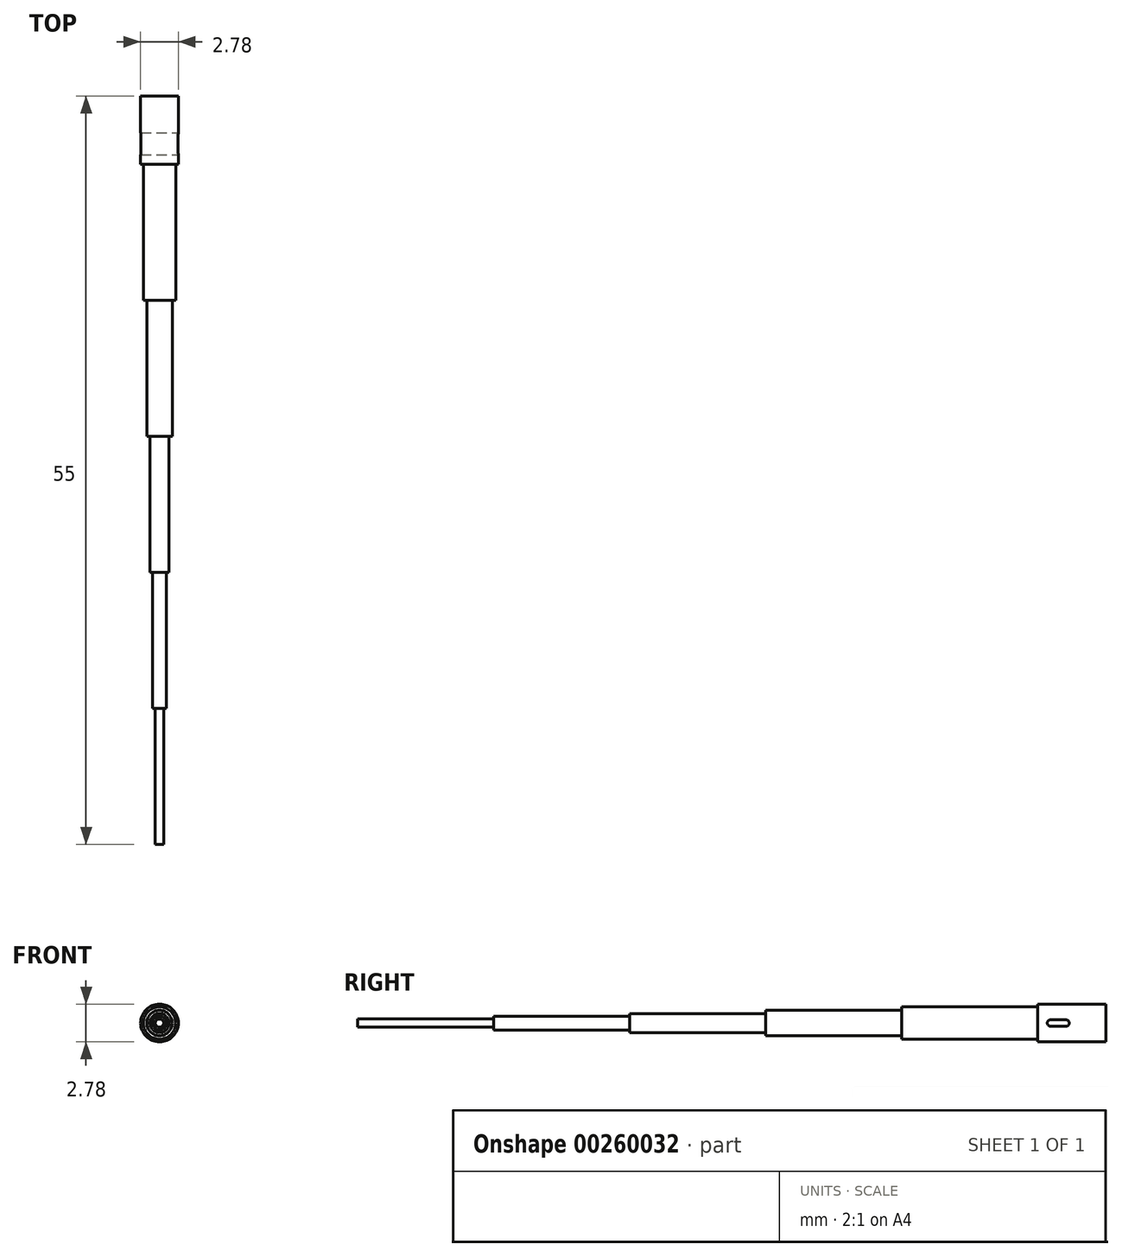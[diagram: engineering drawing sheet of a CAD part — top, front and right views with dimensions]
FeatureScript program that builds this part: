
annotation { "Feature Type Name" : "Feature", "Feature Type Description" : "" }
export const myFeature = defineFeature(function(context is Context, id is Id, definition is map)
    precondition{}
    {
        {
            var Q0;
            Q0=qCreatedBy(makeId("Front.planeOp"),FACE);
            var sketch = newSketch(context, id + "F0", { "sketchPlane" : qUnion([Q0])});
            skCircle(sketch, "E0", {"center": v(0, 0) * mm, "radius": 1.39 * mm});
            skSolve(sketch);
        }
        {
            var Q0;
            Q0 = qSketchRegion(id + "F0", true);
            extrude(context, id + "F1", {"entities" : qUnion([Q0]), "depth" : 5 * mm});
        }
        {
            var Q0;
            Q0=makeQuery(id+"F1.opExtrude","CAP_FACE",FACE,{"disambiguationData":[OSD([sQuery(id+"F0.wireOp",EDGE,"E0")])],"isStart":false});
            var sketch = newSketch(context, id + "F2", { "sketchPlane" : qUnion([Q0])});
            skCircle(sketch, "E1", {"center": v(0, 0) * mm, "radius": 1.19 * mm});
            skSolve(sketch);
        }
        {
            var Q0;
            Q0 = qSketchRegion(id + "F2", true);
            extrude(context, id + "F3", {"entities" : qUnion([Q0]), "operationType" : NewBodyOperationType.ADD, "depth" : 10 * mm});
        }
        {
            var Q0;
            Q0=makeQuery(id+"F3.opExtrude","CAP_FACE",FACE,{"disambiguationData":[OSD([sQuery(id+"F2.wireOp",EDGE,"E1")])],"isStart":false});
            var sketch = newSketch(context, id + "F4", { "sketchPlane" : qUnion([Q0])});
            skCircle(sketch, "E2", {"center": v(0, 0) * mm, "radius": 0.93 * mm});
            skSolve(sketch);
        }
        {
            var Q0;
            Q0 = qSketchRegion(id + "F4", true);
            extrude(context, id + "F5", {"entities" : qUnion([Q0]), "operationType" : NewBodyOperationType.ADD, "depth" : 10 * mm});
        }
        {
            var Q0;
            Q0=makeQuery(id+"F5.opExtrude","CAP_FACE",FACE,{"disambiguationData":[OSD([sQuery(id+"F4.wireOp",EDGE,"E2")])],"isStart":false});
            var sketch = newSketch(context, id + "F6", { "sketchPlane" : qUnion([Q0])});
            skCircle(sketch, "E3", {"center": v(0, 0) * mm, "radius": 0.7 * mm});
            skSolve(sketch);
        }
        {
            var Q0;
            Q0 = qSketchRegion(id + "F6", true);
            extrude(context, id + "F7", {"entities" : qUnion([Q0]), "operationType" : NewBodyOperationType.ADD, "depth" : 10 * mm});
        }
        {
            var Q0;
            Q0=makeQuery(id+"F7.opExtrude","CAP_FACE",FACE,{"disambiguationData":[OSD([sQuery(id+"F6.wireOp",EDGE,"E3")])],"isStart":false});
            var sketch = newSketch(context, id + "F8", { "sketchPlane" : qUnion([Q0])});
            skCircle(sketch, "E4", {"center": v(0, 0) * mm, "radius": 0.5 * mm});
            skSolve(sketch);
        }
        {
            var Q0;
            Q0 = qSketchRegion(id + "F8", true);
            extrude(context, id + "F9", {"entities" : qUnion([Q0]), "operationType" : NewBodyOperationType.ADD, "depth" : 10 * mm});
        }
        {
            var Q0;
            Q0=makeQuery(id+"F9.opExtrude","CAP_FACE",FACE,{"disambiguationData":[OSD([sQuery(id+"F8.wireOp",EDGE,"E4")])],"isStart":false});
            var sketch = newSketch(context, id + "F10", { "sketchPlane" : qUnion([Q0])});
            skCircle(sketch, "E5", {"center": v(0, 0) * mm, "radius": 0.3 * mm});
            skSolve(sketch);
        }
        {
            var Q0;
            Q0 = qSketchRegion(id + "F10", true);
            extrude(context, id + "F11", {"entities" : qUnion([Q0]), "operationType" : NewBodyOperationType.ADD, "depth" : 10 * mm});
        }
        {
            var Q0;
            Q0=qCreatedBy(makeId("Right.planeOp"),FACE);
            var sketch = newSketch(context, id + "F12", { "sketchPlane" : qUnion([Q0])});
            skArc(sketch, "E6", {"start": v(-4.07, 0.23) * mm, "mid": v(-4.3, 0) * mm, "end": v(-4.07, -0.23) * mm});
            skPoint(sketch, "E7.center.orphan", {"position": v(-3.84, 0) * mm});
            skArc(sketch, "E8", {"start": v(-2.9, -0.23) * mm, "mid": v(-2.68, 0) * mm, "end": v(-2.9, 0.23) * mm});
            skPoint(sketch, "E9.center.orphan", {"position": v(-3.6, 0) * mm});
            skPoint(sketch, "E10.center.orphan", {"position": v(-3.14, 0) * mm});
            skPoint(sketch, "E11.center.orphan", {"position": v(-3.37, 0) * mm});
            skLineSegment(sketch, "E12", {"start": v(-2.9, 0.23) * mm, "end": v(-4.07, 0.23) * mm});
            skLineSegment(sketch, "E13", {"start": v(-2.9, -0.23) * mm, "end": v(-4.07, -0.23) * mm});
            skSolve(sketch);
        }
        {
            var Q0;
            Q0 = qSketchRegion(id + "F12", true);
            extrude(context, id + "F13", {"entities" : qUnion([Q0]), "operationType" : NewBodyOperationType.REMOVE, "endBound" : BoundingType.SYMMETRIC, "oppositeDirection" : true, "depth" : 25 * mm});
        }
    });
